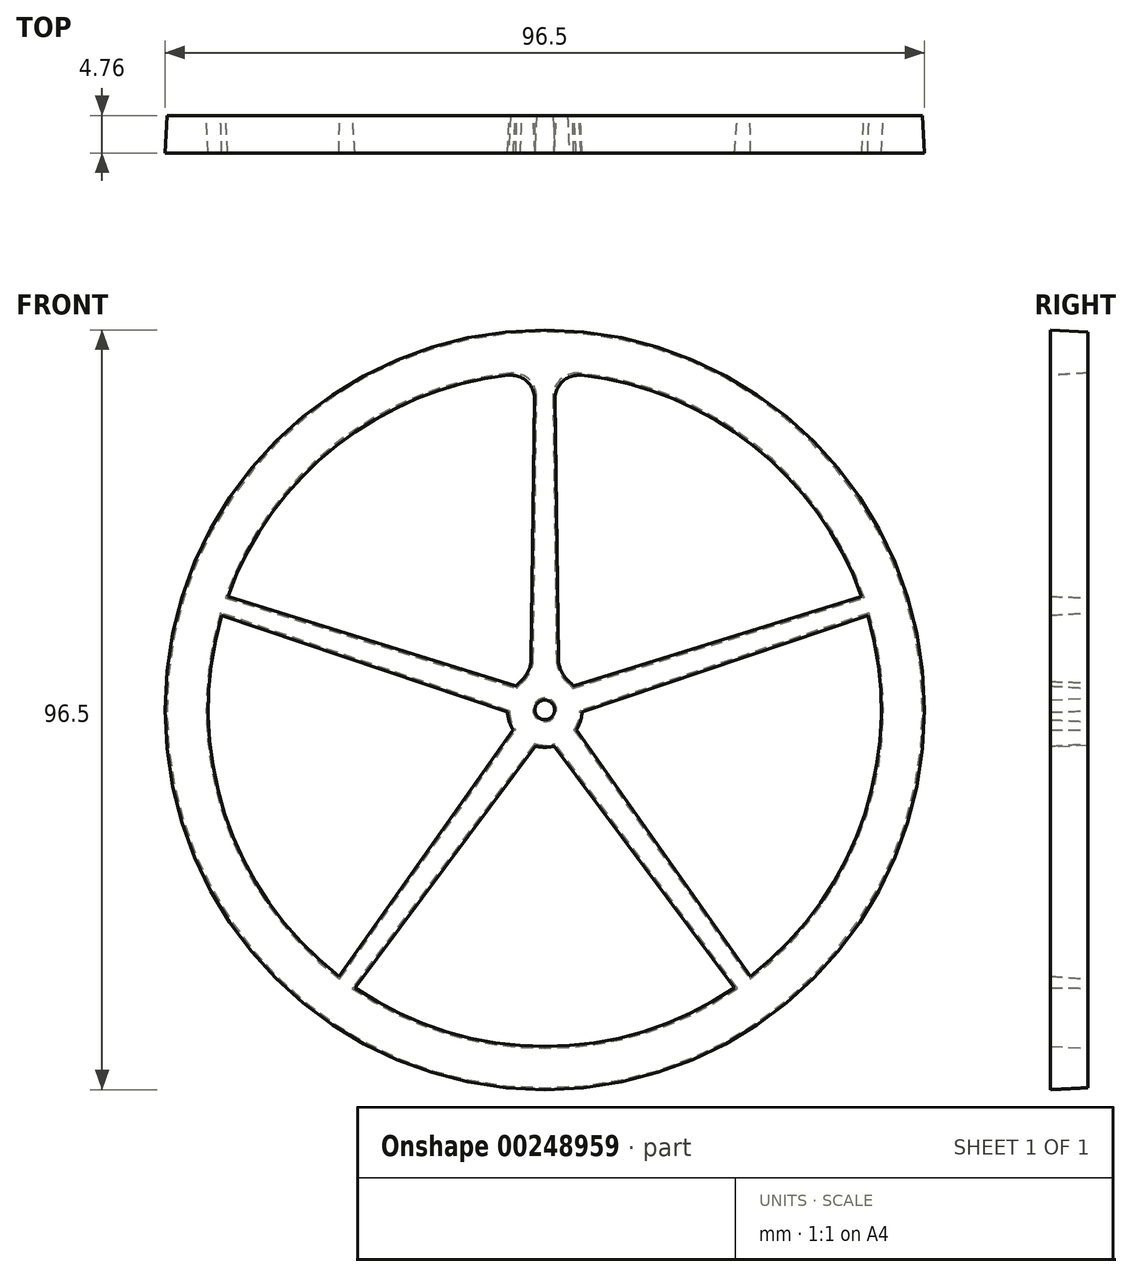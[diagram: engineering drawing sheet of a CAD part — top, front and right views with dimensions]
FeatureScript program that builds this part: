
annotation { "Feature Type Name" : "Feature", "Feature Type Description" : "" }
export const myFeature = defineFeature(function(context is Context, id is Id, definition is map)
    precondition{}
    {
        {
            var Q0;
            Q0=qCreatedBy(makeId("Front.planeOp"),FACE);
            var sketch = newSketch(context, id + "F0", { "sketchPlane" : qUnion([Q0])});
            skCircle(sketch, "E0", {"center": v(0, 0) * mm, "radius": 48 * mm});
            skCircle(sketch, "E1", {"center": v(0, 0) * mm, "radius": 1.5 * mm});
            skCircle(sketch, "E2", {"center": v(0, 0) * mm, "radius": 43 * mm});
            skCircle(sketch, "E3", {"center": v(0, 0) * mm, "radius": 4.5 * mm});
            skLineSegment(sketch, "E4", {"start": v(-1.5, 4.24) * mm, "end": v(-1, 42.99) * mm});
            skLineSegment(sketch, "E5.MirrorCS", {"start": v(1.5, 4.24) * mm, "end": v(1, 42.99) * mm});
            skPoint(sketch, "E6.trimOffspring.end.orphan", {"position": v(0, 43) * mm});
            skPoint(sketch, "E6.trimOffspring.start.orphan", {"position": v(0, 4.5) * mm});
            skSolve(sketch);
        }
        {
            var Q0;
            Q0=makeQuery(id+"F0.imprint","IMPRINT",FACE,{"disambiguationData":[TD([[makeQuery(id+"F0.imprint","IMPRINT",EDGE,{"derivedFrom":sQuery(id+"F0.wireOp",EDGE,"E0")}),1.0]])]});
            var Q1;
            {var subQ0=sQuery(id+"F0.wireOp",EDGE,"E4");Q1=makeQuery(id+"F0.imprint","IMPRINT",FACE,{"disambiguationData":[TD([[makeQuery(id+"F0.imprint","IMPRINT",EDGE,{"derivedFrom":subQ0}),-1.0]])]});}
            var Q2;
            Q2=makeQuery(id+"F0.imprint","IMPRINT",FACE,{"disambiguationData":[TD([[makeQuery(id+"F0.imprint","IMPRINT",EDGE,{"derivedFrom":sQuery(id+"F0.wireOp",EDGE,"E1")}),-1.0]])]});
            var Q3;
            Q3=sQuery(id+"F0.wireOp",EDGE,"E1");
            var Q4;
            Q4=sQuery(id+"F0.wireOp",EDGE,"E0");
            extrude(context, id + "F1", {"entities" : qUnion([Q0, Q1, Q2]), "surfaceEntities" : qUnion([Q3, Q4]), "depth" : 4.76 * mm, "hasDraft" : true, "draftAngle" : 3 * degree});
        }
        {
            var Q0;
            Q0=makeQuery(id+"F1.opExtrude","SWEPT_BODY",BODY,{"disambiguationData":[OSD([sQuery(id+"F0.wireOp",EDGE,"E0"),sQuery(id+"F0.wireOp",EDGE,"E1"),sQuery(id+"F0.wireOp",EDGE,"E2"),sQuery(id+"F0.wireOp",EDGE,"E3"),sQuery(id+"F0.wireOp",EDGE,"E4"),sQuery(id+"F0.wireOp",EDGE,"E5.MirrorCS")])]});
            var Q1;
            Q1=makeQuery(id+"F1.opExtrude","SWEPT_FACE",FACE,{"disambiguationData":[OSD([sQuery(id+"F0.wireOp",EDGE,"E0")])]});
            circularPattern(context, id + "F2", {"operationType" : NewBodyOperationType.ADD, "entities" : qUnion([Q0]), "axis" : qUnion([Q1]), "angle" : 360 * degree, "instanceCount" : 5, "equalSpace" : true});
        }
        {
            var Q0;
            {var subQ0=makeQuery(id+"F1.opExtrude","SWEPT_FACE",FACE,{"disambiguationData":[OSD([sQuery(id+"F0.wireOp",EDGE,"E3")])]});Q0=makeQuery(id+"F2.boolean.opBoolean","INTERSECT",EDGE,{"disambiguationData":[OD(1.0)],"derivedFrom":[makeQuery(id+"F2.opPattern","COPY",FACE,{"derivedFrom":subQ0,"instanceName":"1"}),makeQuery(id+"F2.opPattern","COPY",FACE,{"derivedFrom":subQ0,"instanceName":"2"}),makeQuery(id+"F2.opPattern","COPY",FACE,{"derivedFrom":subQ0,"instanceName":"3"})]});}
            var Q1;
            Q1=makeQuery(id+"F1.opExtrude","SWEPT_EDGE",EDGE,{"disambiguationData":[OSD([sQuery(id+"F0.wireOp",EDGE,"E3"),sQuery(id+"F0.wireOp",EDGE,"E4")])]});
            var Q2;
            Q2=makeQuery(id+"F2.opPattern","COPY",EDGE,{"derivedFrom":makeQuery(id+"F1.opExtrude","SWEPT_EDGE",EDGE,{"disambiguationData":[OSD([sQuery(id+"F0.wireOp",EDGE,"E3"),sQuery(id+"F0.wireOp",EDGE,"E4")])]}),"instanceName":"1"});
            var Q3;
            {var subQ0=makeQuery(id+"F1.opExtrude","SWEPT_FACE",FACE,{"disambiguationData":[OSD([sQuery(id+"F0.wireOp",EDGE,"E3")])]});Q3=makeQuery(id+"F2.boolean.opBoolean","INTERSECT",EDGE,{"disambiguationData":[OD(0.0)],"derivedFrom":[makeQuery(id+"F2.opPattern","COPY",FACE,{"derivedFrom":subQ0,"instanceName":"1"}),makeQuery(id+"F2.opPattern","COPY",FACE,{"derivedFrom":subQ0,"instanceName":"3"})]});}
            var Q4;
            Q4=makeQuery(id+"F1.opExtrude","SWEPT_EDGE",EDGE,{"disambiguationData":[OSD([sQuery(id+"F0.wireOp",EDGE,"E3"),sQuery(id+"F0.wireOp",EDGE,"E5.MirrorCS")])]});
            var Q5;
            Q5=makeQuery(id+"F2.opPattern","COPY",EDGE,{"derivedFrom":makeQuery(id+"F1.opExtrude","SWEPT_EDGE",EDGE,{"disambiguationData":[OSD([sQuery(id+"F0.wireOp",EDGE,"E3"),sQuery(id+"F0.wireOp",EDGE,"E5.MirrorCS")])]}),"instanceName":"1"});
            var Q6;
            {var subQ0=makeQuery(id+"F1.opExtrude","SWEPT_FACE",FACE,{"disambiguationData":[OSD([sQuery(id+"F0.wireOp",EDGE,"E3")])]});Q6=makeQuery(id+"F2.boolean.opBoolean","INTERSECT",EDGE,{"disambiguationData":[OD(0.0)],"derivedFrom":[makeQuery(id+"F2.opPattern","COPY",FACE,{"derivedFrom":subQ0,"instanceName":"1"}),makeQuery(id+"F2.opPattern","COPY",FACE,{"derivedFrom":subQ0,"instanceName":"2"}),makeQuery(id+"F2.opPattern","COPY",FACE,{"derivedFrom":subQ0,"instanceName":"4"})]});}
            var Q7;
            {var subQ0=makeQuery(id+"F1.opExtrude","SWEPT_FACE",FACE,{"disambiguationData":[OSD([sQuery(id+"F0.wireOp",EDGE,"E3")])]});Q7=makeQuery(id+"F2.boolean.opBoolean","INTERSECT",EDGE,{"disambiguationData":[OD(1.0)],"derivedFrom":[makeQuery(id+"F2.opPattern","COPY",FACE,{"derivedFrom":subQ0,"instanceName":"1"}),makeQuery(id+"F2.opPattern","COPY",FACE,{"derivedFrom":subQ0,"instanceName":"3"})]});}
            var Q8;
            {var subQ0=makeQuery(id+"F1.opExtrude","SWEPT_FACE",FACE,{"disambiguationData":[OSD([sQuery(id+"F0.wireOp",EDGE,"E3")])]});Q8=makeQuery(id+"F2.boolean.opBoolean","INTERSECT",EDGE,{"disambiguationData":[OD(0.0)],"derivedFrom":[makeQuery(id+"F2.opPattern","COPY",FACE,{"derivedFrom":subQ0,"instanceName":"1"}),makeQuery(id+"F2.opPattern","COPY",FACE,{"derivedFrom":subQ0,"instanceName":"2"}),makeQuery(id+"F2.opPattern","COPY",FACE,{"derivedFrom":subQ0,"instanceName":"3"})]});}
            var Q9;
            {var subQ0=makeQuery(id+"F1.opExtrude","SWEPT_FACE",FACE,{"disambiguationData":[OSD([sQuery(id+"F0.wireOp",EDGE,"E3")])]});Q9=makeQuery(id+"F2.boolean.opBoolean","INTERSECT",EDGE,{"disambiguationData":[OD(1.0)],"derivedFrom":[makeQuery(id+"F2.opPattern","COPY",FACE,{"derivedFrom":subQ0,"instanceName":"1"}),makeQuery(id+"F2.opPattern","COPY",FACE,{"derivedFrom":subQ0,"instanceName":"2"}),makeQuery(id+"F2.opPattern","COPY",FACE,{"derivedFrom":subQ0,"instanceName":"4"})]});}
            fillet(context, id + "F3", {"entities" : qUnion([Q0, Q1, Q2, Q3, Q4, Q5, Q6, Q7, Q8, Q9]), "radius" : 4 * mm, "tangentPropagation" : true, "allowEdgeOverflow" : false});
        }
        {
            var Q0;
            {var subQ0=makeQuery(id+"F1.opExtrude","SWEPT_FACE",FACE,{"disambiguationData":[OSD([sQuery(id+"F0.wireOp",EDGE,"E2")])]});Q0=makeQuery(id+"F2.boolean.opBoolean","INTERSECT",EDGE,{"disambiguationData":[OD(1.0)],"derivedFrom":[makeQuery(id+"F2.opPattern","COPY",FACE,{"derivedFrom":subQ0,"instanceName":"1"}),makeQuery(id+"F2.opPattern","COPY",FACE,{"derivedFrom":subQ0,"instanceName":"3"})]});}
            var Q1;
            {var subQ0=makeQuery(id+"F1.opExtrude","SWEPT_FACE",FACE,{"disambiguationData":[OSD([sQuery(id+"F0.wireOp",EDGE,"E2")])]});Q1=makeQuery(id+"F2.boolean.opBoolean","INTERSECT",EDGE,{"disambiguationData":[OD(1.0)],"derivedFrom":[makeQuery(id+"F2.opPattern","COPY",FACE,{"derivedFrom":subQ0,"instanceName":"1"}),makeQuery(id+"F2.opPattern","COPY",FACE,{"derivedFrom":subQ0,"instanceName":"2"}),makeQuery(id+"F2.opPattern","COPY",FACE,{"derivedFrom":subQ0,"instanceName":"4"})]});}
            var Q2;
            {var subQ0=makeQuery(id+"F1.opExtrude","SWEPT_FACE",FACE,{"disambiguationData":[OSD([sQuery(id+"F0.wireOp",EDGE,"E2")])]});Q2=makeQuery(id+"F2.boolean.opBoolean","INTERSECT",EDGE,{"disambiguationData":[OD(1.0)],"derivedFrom":[makeQuery(id+"F2.opPattern","COPY",FACE,{"derivedFrom":subQ0,"instanceName":"1"}),makeQuery(id+"F2.opPattern","COPY",FACE,{"derivedFrom":subQ0,"instanceName":"2"}),makeQuery(id+"F2.opPattern","COPY",FACE,{"derivedFrom":subQ0,"instanceName":"3"})]});}
            var Q3;
            Q3=makeQuery(id+"F2.opPattern","COPY",EDGE,{"derivedFrom":makeQuery(id+"F1.opExtrude","SWEPT_EDGE",EDGE,{"disambiguationData":[OSD([sQuery(id+"F0.wireOp",EDGE,"E2"),sQuery(id+"F0.wireOp",EDGE,"E4")])]}),"instanceName":"1"});
            var Q4;
            Q4=makeQuery(id+"F2.opPattern","COPY",EDGE,{"derivedFrom":makeQuery(id+"F1.opExtrude","SWEPT_EDGE",EDGE,{"disambiguationData":[OSD([sQuery(id+"F0.wireOp",EDGE,"E2"),sQuery(id+"F0.wireOp",EDGE,"E5.MirrorCS")])]}),"instanceName":"1"});
            var Q5;
            {var subQ0=makeQuery(id+"F1.opExtrude","SWEPT_FACE",FACE,{"disambiguationData":[OSD([sQuery(id+"F0.wireOp",EDGE,"E2")])]});Q5=makeQuery(id+"F2.boolean.opBoolean","INTERSECT",EDGE,{"disambiguationData":[OD(0.0)],"derivedFrom":[makeQuery(id+"F2.opPattern","COPY",FACE,{"derivedFrom":subQ0,"instanceName":"1"}),makeQuery(id+"F2.opPattern","COPY",FACE,{"derivedFrom":subQ0,"instanceName":"3"})]});}
            var Q6;
            {var subQ0=makeQuery(id+"F1.opExtrude","SWEPT_FACE",FACE,{"disambiguationData":[OSD([sQuery(id+"F0.wireOp",EDGE,"E2")])]});Q6=makeQuery(id+"F2.boolean.opBoolean","INTERSECT",EDGE,{"disambiguationData":[OD(0.0)],"derivedFrom":[makeQuery(id+"F2.opPattern","COPY",FACE,{"derivedFrom":subQ0,"instanceName":"1"}),makeQuery(id+"F2.opPattern","COPY",FACE,{"derivedFrom":subQ0,"instanceName":"2"}),makeQuery(id+"F2.opPattern","COPY",FACE,{"derivedFrom":subQ0,"instanceName":"4"})]});}
            var Q7;
            {var subQ0=makeQuery(id+"F1.opExtrude","SWEPT_FACE",FACE,{"disambiguationData":[OSD([sQuery(id+"F0.wireOp",EDGE,"E2")])]});Q7=makeQuery(id+"F2.boolean.opBoolean","INTERSECT",EDGE,{"disambiguationData":[OD(0.0)],"derivedFrom":[makeQuery(id+"F2.opPattern","COPY",FACE,{"derivedFrom":subQ0,"instanceName":"1"}),makeQuery(id+"F2.opPattern","COPY",FACE,{"derivedFrom":subQ0,"instanceName":"2"}),makeQuery(id+"F2.opPattern","COPY",FACE,{"derivedFrom":subQ0,"instanceName":"3"})]});}
            var Q8;
            Q8=makeQuery(id+"F1.opExtrude","SWEPT_EDGE",EDGE,{"disambiguationData":[OSD([sQuery(id+"F0.wireOp",EDGE,"E2"),sQuery(id+"F0.wireOp",EDGE,"E4")])]});
            var Q9;
            Q9=makeQuery(id+"F1.opExtrude","SWEPT_EDGE",EDGE,{"disambiguationData":[OSD([sQuery(id+"F0.wireOp",EDGE,"E2"),sQuery(id+"F0.wireOp",EDGE,"E5.MirrorCS")])]});
            fillet(context, id + "F4", {"entities" : qUnion([Q0, Q1, Q2, Q3, Q4, Q5, Q6, Q7, Q8, Q9]), "radius" : 3 * mm, "tangentPropagation" : true, "allowEdgeOverflow" : false});
        }
    });
